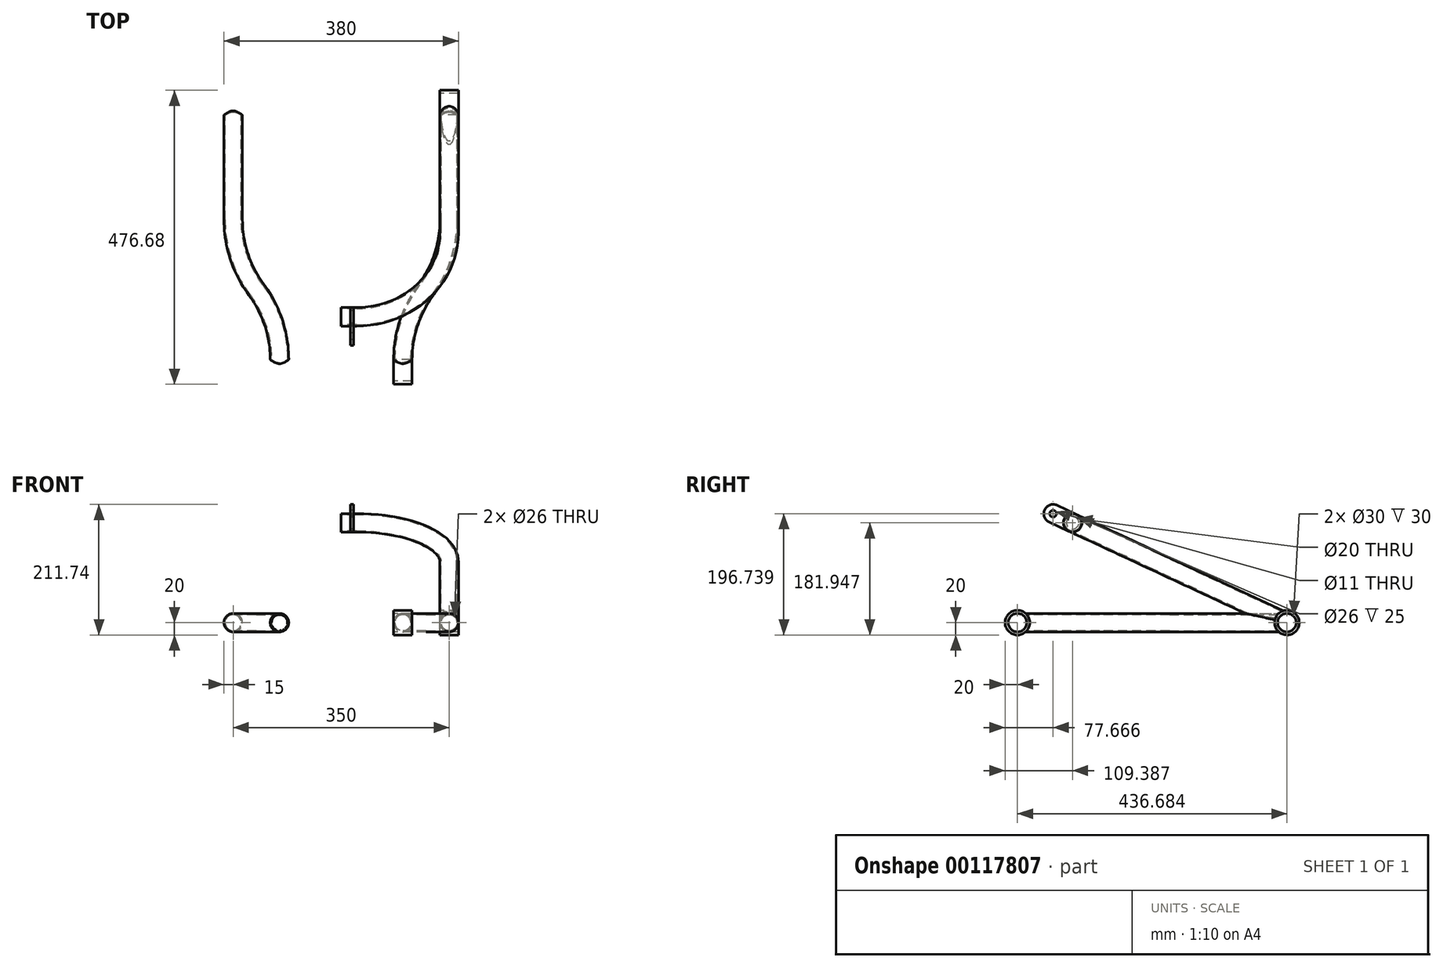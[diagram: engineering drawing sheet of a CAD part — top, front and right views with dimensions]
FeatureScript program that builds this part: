
annotation { "Feature Type Name" : "Feature", "Feature Type Description" : "" }
export const myFeature = defineFeature(function(context is Context, id is Id, definition is map)
    precondition{}
    {
        {
            var Q0;
            Q0=qCreatedBy(makeId("Top.planeOp"),FACE);
            var sketch = newSketch(context, id + "F0", { "sketchPlane" : qUnion([Q0])});
            skLineSegment(sketch, "E0", {"start": v(-251.36, 436.68) * mm, "end": v(249.52, 436.68) * mm, "construction": true});
            skLineSegment(sketch, "E1", {"start": v(-235.2, 113.48) * mm, "end": v(252.22, 113.48) * mm, "construction": true});
            skPoint(sketch, "E2.startSnap0", {"position": v(8.5, 113.48) * mm});
            skLineSegment(sketch, "E3.0", {"start": v(-235.2, 63.48) * mm, "end": v(252.22, 63.48) * mm, "construction": true});
            skLineSegment(sketch, "E4.bottom", {"start": v(85, 20) * mm, "end": v(115, 20) * mm});
            skLineSegment(sketch, "E4.top", {"start": v(85, 0) * mm, "end": v(115, 0) * mm});
            skLineSegment(sketch, "E4.left", {"start": v(85, 20) * mm, "end": v(85, 0) * mm});
            skLineSegment(sketch, "E4.right", {"start": v(115, 20) * mm, "end": v(115, 0) * mm});
            skArc(sketch, "E5", {"start": v(100, 20) * mm, "mid": v(109.62, 79.69) * mm, "end": v(137.5, 133.33) * mm});
            skArc(sketch, "E6", {"start": v(137.5, 133.33) * mm, "mid": v(165.38, 186.97) * mm, "end": v(175, 246.66) * mm});
            skLineSegment(sketch, "E7", {"start": v(175, 246.66) * mm, "end": v(175, 436.68) * mm});
            skLineSegment(sketch, "E8", {"start": v(100, 20) * mm, "end": v(100, 0) * mm});
            skPoint(sketch, "E8.endSnap0", {"position": v(100, 0) * mm});
            skLineSegment(sketch, "E9", {"start": v(160, 436.68) * mm, "end": v(160, 416.68) * mm});
            skLineSegment(sketch, "E10", {"start": v(160, 416.68) * mm, "end": v(190, 416.68) * mm});
            skLineSegment(sketch, "E11", {"start": v(190, 416.68) * mm, "end": v(190, 436.68) * mm});
            skLineSegment(sketch, "E12", {"start": v(190, 436.68) * mm, "end": v(160, 436.68) * mm});
            skSolve(sketch);
        }
        {
            var Q0;
            Q0=qCreatedBy(makeId("Front.planeOp"),FACE);
            var sketch = newSketch(context, id + "F1", { "sketchPlane" : qUnion([Q0])});
            skPoint(sketch, "E13.0", {"position": v(100, 0) * mm});
            skCircle(sketch, "E14", {"center": v(100, 0) * mm, "radius": 15 * mm});
            skSolve(sketch);
        }
        {
            var Q0;
            Q0=makeQuery(id+"F1.imprint","IMPRINT",FACE,{"disambiguationData":[TD([[makeQuery(id+"F1.imprint","IMPRINT",EDGE,{"derivedFrom":sQuery(id+"F1.wireOp",EDGE,"E14")}),1.0]])]});
            var Q1;
            Q1=sQuery(id+"F0.wireOp",EDGE,"E8");
            var Q2;
            Q2=sQuery(id+"F0.wireOp",EDGE,"E5");
            var Q3;
            Q3=sQuery(id+"F0.wireOp",EDGE,"E6");
            var Q4;
            Q4=sQuery(id+"F0.wireOp",EDGE,"E7");
            sweep(context, id + "F2", {"profiles" : qUnion([Q0]), "path" : qUnion([Q1, Q2, Q3, Q4])});
        }
        {
            var Q0;
            {var subQ0=sQuery(id+"F0.wireOp",EDGE,"E4.left");Q0=makeQuery(id+"F0.imprint","IMPRINT",FACE,{"disambiguationData":[TD([[makeQuery(id+"F0.imprint","IMPRINT",EDGE,{"derivedFrom":subQ0}),1.0]])]});}
            var Q1;
            {var subQ0=sQuery(id+"F0.wireOp",EDGE,"E4.right");Q1=makeQuery(id+"F0.imprint","IMPRINT",FACE,{"disambiguationData":[TD([[makeQuery(id+"F0.imprint","IMPRINT",EDGE,{"derivedFrom":subQ0}),-1.0]])]});}
            var Q2;
            Q2=sQuery(id+"F0.wireOp",EDGE,"E4.top");
            revolve(context, id + "F3", {"entities" : qUnion([Q0, Q1]), "axis" : qUnion([Q2]), "revolveType" : RevolveType.FULL});
        }
        {
            var Q0;
            {var subQ5=sQuery(id+"F0.wireOp",EDGE,"E9");Q0=makeQuery(id+"F0.imprint","IMPRINT",FACE,{"disambiguationData":[TD([[makeQuery(id+"F0.imprint","IMPRINT",EDGE,{"derivedFrom":subQ5}),1.0]])]});}
            var Q1;
            {var subQ5=sQuery(id+"F0.wireOp",EDGE,"E11");Q1=makeQuery(id+"F0.imprint","IMPRINT",FACE,{"disambiguationData":[TD([[makeQuery(id+"F0.imprint","IMPRINT",EDGE,{"derivedFrom":subQ5}),1.0]])]});}
            var Q2;
            Q2=sQuery(id+"F0.wireOp",EDGE,"E0");
            revolve(context, id + "F4", {"entities" : qUnion([Q0, Q1]), "axis" : qUnion([Q2]), "revolveType" : RevolveType.FULL});
        }
        {
            var Q0;
            Q0=sQuery(id+"F0.wireOp",EDGE,"E0");
            var Q1;
            Q1=qCreatedBy(makeId("Top.planeOp"),FACE);
            cPlane(context, id + "F5", {"entities" : qUnion([Q0, Q1]), "cplaneType" : CPlaneType.LINE_ANGLE, "offset" : 25 * mm, "angle" : 335 * degree, "width" : 150 * mm, "height" : 150 * mm});
        }
        {
            var Q0;
            Q0=qCreatedBy(id+"F5.planeOp",FACE);
            var sketch = newSketch(context, id + "F6", { "sketchPlane" : qUnion([Q0])});
            skLineSegment(sketch, "E15.0", {"start": v(-251.36, -12.57) * mm, "end": v(251.36, -12.57) * mm, "construction": true});
            skPoint(sketch, "E16.startSnap0", {"position": v(0, -12.57) * mm});
            skLineSegment(sketch, "E17.0", {"start": v(175, -223.55) * mm, "end": v(175, -395.77) * mm, "construction": true});
            skLineSegment(sketch, "E18", {"start": v(175, -162.57) * mm, "end": v(175, -395.77) * mm});
            skLineSegment(sketch, "E19", {"start": v(0, -12.57) * mm, "end": v(25, -12.57) * mm});
            skArc(sketch, "E20", {"start": v(25, -12.57) * mm, "mid": v(131.07, -56.5) * mm, "end": v(175, -162.57) * mm});
            skSolve(sketch);
        }
        {
            var Q0;
            Q0=sQuery(id+"F0.wireOp",EDGE,"E0");
            var Q1;
            Q1=qCreatedBy(id+"F5.planeOp",FACE);
            cPlane(context, id + "F7", {"entities" : qUnion([Q0, Q1]), "cplaneType" : CPlaneType.LINE_ANGLE, "offset" : 25 * mm, "angle" : 90 * degree, "width" : 150 * mm, "height" : 150 * mm});
        }
        {
            var Q0;
            Q0=qCreatedBy(id+"F7.planeOp",FACE);
            var sketch = newSketch(context, id + "F8", { "sketchPlane" : qUnion([Q0])});
            skPoint(sketch, "E21.0", {"position": v(175, 184.55) * mm});
            skCircle(sketch, "E22", {"center": v(175, 184.55) * mm, "radius": 15 * mm});
            skSolve(sketch);
        }
        {
            var Q0;
            Q0 = qSketchRegion(id + "F8", true);
            var Q1;
            Q1 = qConstructionFilter(qBodyType(qCreatedBy(id + "F6" ,EDGE), BodyType.WIRE), ConstructionObject.NO);
            sweep(context, id + "F9", {"profiles" : qUnion([Q0]), "path" : qUnion([Q1])});
        }
        {
            var Q0;
            Q0=qCreatedBy(makeId("Right.planeOp"),FACE);
            cPlane(context, id + "F10", {"entities" : qUnion([Q0]), "cplaneType" : CPlaneType.OFFSET, "offset" : 15 * mm, "width" : 150 * mm, "height" : 150 * mm});
        }
        {
            var Q0;
            Q0=qCreatedBy(id+"F10.planeOp",FACE);
            var sketch = newSketch(context, id + "F11", { "sketchPlane" : qUnion([Q0])});
            skPoint(sketch, "E23.0", {"position": v(89.39, 161.95) * mm});
            skCircle(sketch, "E24", {"center": v(89.39, 161.95) * mm, "radius": 10 * mm});
            skArc(sketch, "E25", {"start": v(83.05, 148.35) * mm, "mid": v(102.98, 155.6) * mm, "end": v(95.73, 175.54) * mm});
            skLineSegment(sketch, "E26", {"start": v(51.33, 163.14) * mm, "end": v(83.05, 148.35) * mm});
            skLineSegment(sketch, "E27", {"start": v(95.73, 175.54) * mm, "end": v(64, 190.33) * mm});
            skArc(sketch, "E28.trimOffspring", {"start": v(64, 190.33) * mm, "mid": v(44.07, 183.08) * mm, "end": v(51.33, 163.14) * mm});
            skLineSegment(sketch, "E29", {"start": v(89.39, 161.95) * mm, "end": v(57.67, 176.74) * mm, "construction": true});
            skCircle(sketch, "E30", {"center": v(57.67, 176.74) * mm, "radius": 5.5 * mm});
            skSolve(sketch);
        }
        {
            var Q0;
            Q0=makeQuery(id+"F11.imprint","IMPRINT",FACE,{"disambiguationData":[TD([[makeQuery(id+"F11.imprint","IMPRINT",EDGE,{"derivedFrom":sQuery(id+"F11.wireOp",EDGE,"E25")}),1.0]])]});
            extrude(context, id + "F12", {"entities" : qUnion([Q0]), "depth" : 5 * mm});
        }
        {
            var Q0;
            Q0=makeQuery(id+"F4.opRevolve","SWEPT_BODY",BODY,{"disambiguationData":[OSD([sQuery(id+"F0.wireOp",EDGE,"E9"),sQuery(id+"F0.wireOp",EDGE,"E10"),sQuery(id+"F0.wireOp",EDGE,"E11"),sQuery(id+"F0.wireOp",EDGE,"E12")])]});
            var Q1;
            Q1=makeQuery(id+"F3.opRevolve","SWEPT_BODY",BODY,{"disambiguationData":[OSD([sQuery(id+"F0.wireOp",EDGE,"E4.bottom"),sQuery(id+"F0.wireOp",EDGE,"E4.top"),sQuery(id+"F0.wireOp",EDGE,"E4.left"),sQuery(id+"F0.wireOp",EDGE,"E4.right")])]});
            var Q2;
            Q2=makeQuery(id+"F2.opSweep","SWEPT_BODY",BODY,{"disambiguationData":[OSD([sQuery(id+"F0.wireOp",EDGE,"E7"),sQuery(id+"F1.wireOp",EDGE,"E14")])]});
            booleanBodies(context, id + "F13", {"operationType" : BooleanOperationType.SUBTRACTION, "tools" : qUnion([Q0, Q1]), "targets" : qUnion([Q2]), "keepTools" : true});
        }
        {
            var Q0;
            Q0=makeQuery(id+"FYztzqkWfeWl253_2.opSweep","SWEPT_BODY",BODY,{"disambiguationData":[OSD([sQuery(id+"F0.wireOp",EDGE,"E7"),sQuery(id+"F1.wireOp",EDGE,"E14")])]});
            var Q1;
            Q1=makeQuery(id+"F4.opRevolve","SWEPT_BODY",BODY,{"disambiguationData":[OSD([sQuery(id+"F0.wireOp",EDGE,"E9"),sQuery(id+"F0.wireOp",EDGE,"E10"),sQuery(id+"F0.wireOp",EDGE,"E11"),sQuery(id+"F0.wireOp",EDGE,"E12")])]});
            var Q2;
            Q2=makeQuery(id+"F9.opSweep","SWEPT_BODY",BODY,{"disambiguationData":[OSD([sQuery(id+"F6.wireOp",EDGE,"E18"),sQuery(id+"F8.wireOp",EDGE,"E22")])]});
            booleanBodies(context, id + "F14", {"operationType" : BooleanOperationType.SUBTRACTION, "tools" : qUnion([Q0, Q1]), "targets" : qUnion([Q2]), "keepTools" : true});
        }
        {
            var Q0;
            Q0=makeQuery(id+"F2.opSweep","SWEPT_BODY",BODY,{"disambiguationData":[OSD([sQuery(id+"F0.wireOp",EDGE,"E7"),sQuery(id+"F1.wireOp",EDGE,"E14")])]});
            var Q1;
            Q1=makeQuery(id+"F9.opSweep","SWEPT_BODY",BODY,{"disambiguationData":[OSD([sQuery(id+"F6.wireOp",EDGE,"E18"),sQuery(id+"F8.wireOp",EDGE,"E22")])]});
            booleanBodies(context, id + "F15", {"operationType" : BooleanOperationType.SUBTRACTION, "tools" : qUnion([Q0]), "targets" : qUnion([Q1]), "keepTools" : true});
        }
        {
            var Q0;
            Q0=makeQuery(id+"F14.opBoolean","COPY",FACE,{"derivedFrom":makeQuery(id+"FYztzqkWfeWl253_2.opSweep","SWEPT_FACE",FACE,{"disambiguationData":[OSD([sQuery(id+"F0.wireOp",EDGE,"E7"),sQuery(id+"F1.wireOp",EDGE,"E14")])]})});
            var Q1;
            Q1=makeQuery(id+"F14.opBoolean","COPY",FACE,{"derivedFrom":makeQuery(id+"F4.opRevolve","SWEPT_FACE",FACE,{"disambiguationData":[OSD([sQuery(id+"F0.wireOp",EDGE,"E10")])]})});
            var Q2;
            Q2=makeQuery(id+"F15.opBoolean","COPY",FACE,{"derivedFrom":makeQuery(id+"F2.opSweep","SWEPT_FACE",FACE,{"disambiguationData":[OSD([sQuery(id+"F0.wireOp",EDGE,"E7"),sQuery(id+"F1.wireOp",EDGE,"E14")])]})});
            var Q3;
            Q3=makeQuery(id+"F9.opSweep","CAP_FACE",FACE,{"disambiguationData":[OSD([sQuery(id+"F6.wireOp",VERTEX,"E19.start"),sQuery(id+"F8.wireOp",EDGE,"E22")])],"isStart":false});
            shell(context, id + "F16", {"entities" : qUnion([Q0, Q1, Q2, Q3]), "thickness" : 2 * mm});
        }
        {
            var Q0;
            Q0=makeQuery(id+"FRPU5REYNNxk64H_2.opBoolean","COPY",FACE,{"derivedFrom":makeQuery(id+"F9.opSweep","SWEPT_FACE",FACE,{"disambiguationData":[OSD([sQuery(id+"F6.wireOp",EDGE,"E18"),sQuery(id+"F8.wireOp",EDGE,"E22")])]})});
            var Q1;
            Q1=makeQuery(id+"F13.opBoolean","COPY",FACE,{"derivedFrom":makeQuery(id+"F4.opRevolve","SWEPT_FACE",FACE,{"disambiguationData":[OSD([sQuery(id+"F0.wireOp",EDGE,"E10")])]})});
            var Q2;
            Q2=makeQuery(id+"F13.opBoolean","COPY",FACE,{"derivedFrom":makeQuery(id+"F3.opRevolve","SWEPT_FACE",FACE,{"disambiguationData":[OSD([sQuery(id+"F0.wireOp",EDGE,"E4.bottom")])]})});
            shell(context, id + "F17", {"entities" : qUnion([Q0, Q1, Q2]), "thickness" : 2 * mm});
        }
        {
            var Q0;
            Q0=makeQuery(id+"F3.opRevolve","SWEPT_FACE",FACE,{"disambiguationData":[OSD([sQuery(id+"F0.wireOp",EDGE,"E4.right")])]});
            var Q1;
            Q1=makeQuery(id+"F4.opRevolve","SWEPT_FACE",FACE,{"disambiguationData":[OSD([sQuery(id+"F0.wireOp",EDGE,"E11")])]});
            var Q2;
            Q2=makeQuery(id+"F4.opRevolve","SWEPT_FACE",FACE,{"disambiguationData":[OSD([sQuery(id+"F0.wireOp",EDGE,"E9")])]});
            var Q3;
            Q3=makeQuery(id+"F3.opRevolve","SWEPT_FACE",FACE,{"disambiguationData":[OSD([sQuery(id+"F0.wireOp",EDGE,"E4.left")])]});
            shell(context, id + "F18", {"entities" : qUnion([Q0, Q1, Q2, Q3]), "thickness" : 5 * mm});
        }
        {
            var Q0;
            Q0=makeQuery(id+"F2.opSweep","SWEPT_BODY",BODY,{"disambiguationData":[OSD([sQuery(id+"F0.wireOp",EDGE,"E7"),sQuery(id+"F1.wireOp",EDGE,"E14")])]});
            var Q1;
            Q1=qCreatedBy(makeId("Right.planeOp"),FACE);
            mirror(context, id + "F19", {"operationType" : NewBodyOperationType.ADD, "entities" : qUnion([Q0]), "mirrorPlane" : qUnion([Q1])});
        }
    });
